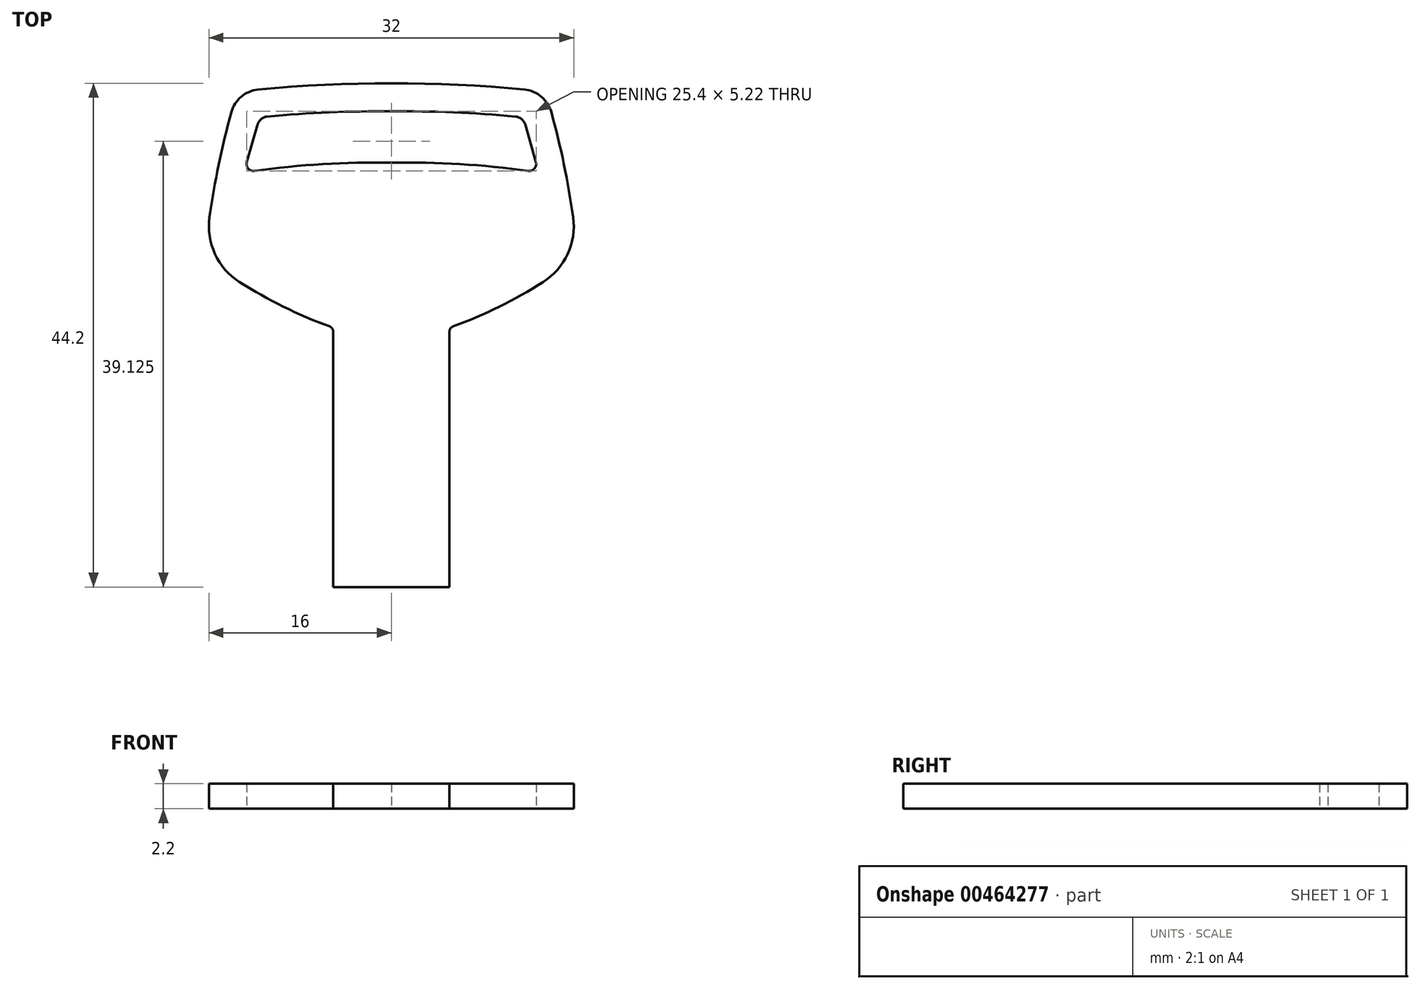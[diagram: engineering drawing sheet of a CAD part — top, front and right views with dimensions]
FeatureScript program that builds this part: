
annotation { "Feature Type Name" : "Feature", "Feature Type Description" : "" }
export const myFeature = defineFeature(function(context is Context, id is Id, definition is map)
    precondition{}
    {
        {
            var Q0;
            Q0=qCreatedBy(makeId("Top.planeOp"),FACE);
            var sketch = newSketch(context, id + "F0", { "sketchPlane" : qUnion([Q0])});
            skArc(sketch, "E0", {"start": v(11.68, 21.24) * mm, "mid": v(5.85, 21.66) * mm, "end": v(0, 21.8) * mm});
            skArc(sketch, "E1", {"start": v(14.03, 19.27) * mm, "mid": v(13.16, 20.62) * mm, "end": v(11.68, 21.24) * mm});
            skArc(sketch, "E2", {"start": v(15.94, 10.05) * mm, "mid": v(15.14, 14.7) * mm, "end": v(14.03, 19.27) * mm});
            skArc(sketch, "E3", {"start": v(13.32, 4.37) * mm, "mid": v(15.47, 6.82) * mm, "end": v(15.94, 10.05) * mm});
            skArc(sketch, "E4", {"start": v(5.43, 0.47) * mm, "mid": v(9.48, 2.2) * mm, "end": v(13.32, 4.37) * mm});
            skArc(sketch, "E5", {"start": v(5.43, 0.47) * mm, "mid": v(5.2, 0.29) * mm, "end": v(5.1, 0) * mm});
            skLineSegment(sketch, "E6", {"start": v(5.1, 0) * mm, "end": v(5.1, -22.4) * mm});
            skArc(sketch, "E7", {"start": v(11.74, 18.16) * mm, "mid": v(11.42, 18.65) * mm, "end": v(10.88, 18.88) * mm});
            skArc(sketch, "E8", {"start": v(12.02, 14.11) * mm, "mid": v(12.56, 14.32) * mm, "end": v(12.68, 14.87) * mm});
            skArc(sketch, "E9", {"start": v(12.02, 14.11) * mm, "mid": v(6.02, 14.7) * mm, "end": v(0, 14.84) * mm});
            skLineSegment(sketch, "E10", {"start": v(11.74, 18.16) * mm, "end": v(12.68, 14.87) * mm});
            skArc(sketch, "E11.MirrorCS", {"start": v(-11.74, 18.16) * mm, "mid": v(-11.42, 18.65) * mm, "end": v(-10.88, 18.88) * mm});
            skArc(sketch, "E12.MirrorCS", {"start": v(-5.43, 0.47) * mm, "mid": v(-5.2, 0.29) * mm, "end": v(-5.1, 0) * mm});
            skArc(sketch, "E13.MirrorCS", {"start": v(-12.02, 14.11) * mm, "mid": v(-12.56, 14.32) * mm, "end": v(-12.68, 14.87) * mm});
            skArc(sketch, "E14.MirrorCS", {"start": v(-12.02, 14.11) * mm, "mid": v(-6.02, 14.7) * mm, "end": v(0, 14.84) * mm});
            skLineSegment(sketch, "E15.MirrorCS", {"start": v(-11.74, 18.16) * mm, "end": v(-12.68, 14.87) * mm});
            skArc(sketch, "E16.MirrorCS", {"start": v(-14.03, 19.27) * mm, "mid": v(-13.16, 20.62) * mm, "end": v(-11.68, 21.24) * mm});
            skArc(sketch, "E17.MirrorCS", {"start": v(-11.68, 21.24) * mm, "mid": v(-5.85, 21.66) * mm, "end": v(0, 21.8) * mm});
            skLineSegment(sketch, "E18.MirrorCS", {"start": v(-5.1, 0) * mm, "end": v(-5.1, -22.4) * mm});
            skArc(sketch, "E19.MirrorCS", {"start": v(-15.94, 10.05) * mm, "mid": v(-15.14, 14.7) * mm, "end": v(-14.03, 19.27) * mm});
            skArc(sketch, "E20.MirrorCS", {"start": v(-13.32, 4.37) * mm, "mid": v(-15.47, 6.82) * mm, "end": v(-15.94, 10.05) * mm});
            skArc(sketch, "E21.MirrorCS", {"start": v(-5.43, 0.47) * mm, "mid": v(-9.48, 2.2) * mm, "end": v(-13.32, 4.37) * mm});
            skArc(sketch, "E22", {"start": v(10.88, 18.88) * mm, "mid": v(5.44, 19.25) * mm, "end": v(0, 19.33) * mm});
            skArc(sketch, "E23.MirrorCS", {"start": v(-10.88, 18.88) * mm, "mid": v(-5.44, 19.25) * mm, "end": v(0, 19.33) * mm});
            skLineSegment(sketch, "E24", {"start": v(5.1, -22.4) * mm, "end": v(-5.1, -22.4) * mm});
            skSolve(sketch);
        }
        {
            var Q0;
            Q0=makeQuery(id+"F0.imprint","IMPRINT",FACE,{"disambiguationData":[TD([[makeQuery(id+"F0.imprint","IMPRINT",EDGE,{"derivedFrom":sQuery(id+"F0.wireOp",EDGE,"E0")}),1.0]])]});
            extrude(context, id + "F1", {"entities" : qUnion([Q0]), "endBound" : BoundingType.SYMMETRIC, "depth" : 2.2 * mm, "offsetDistance" : 25 * mm});
        }
    });
